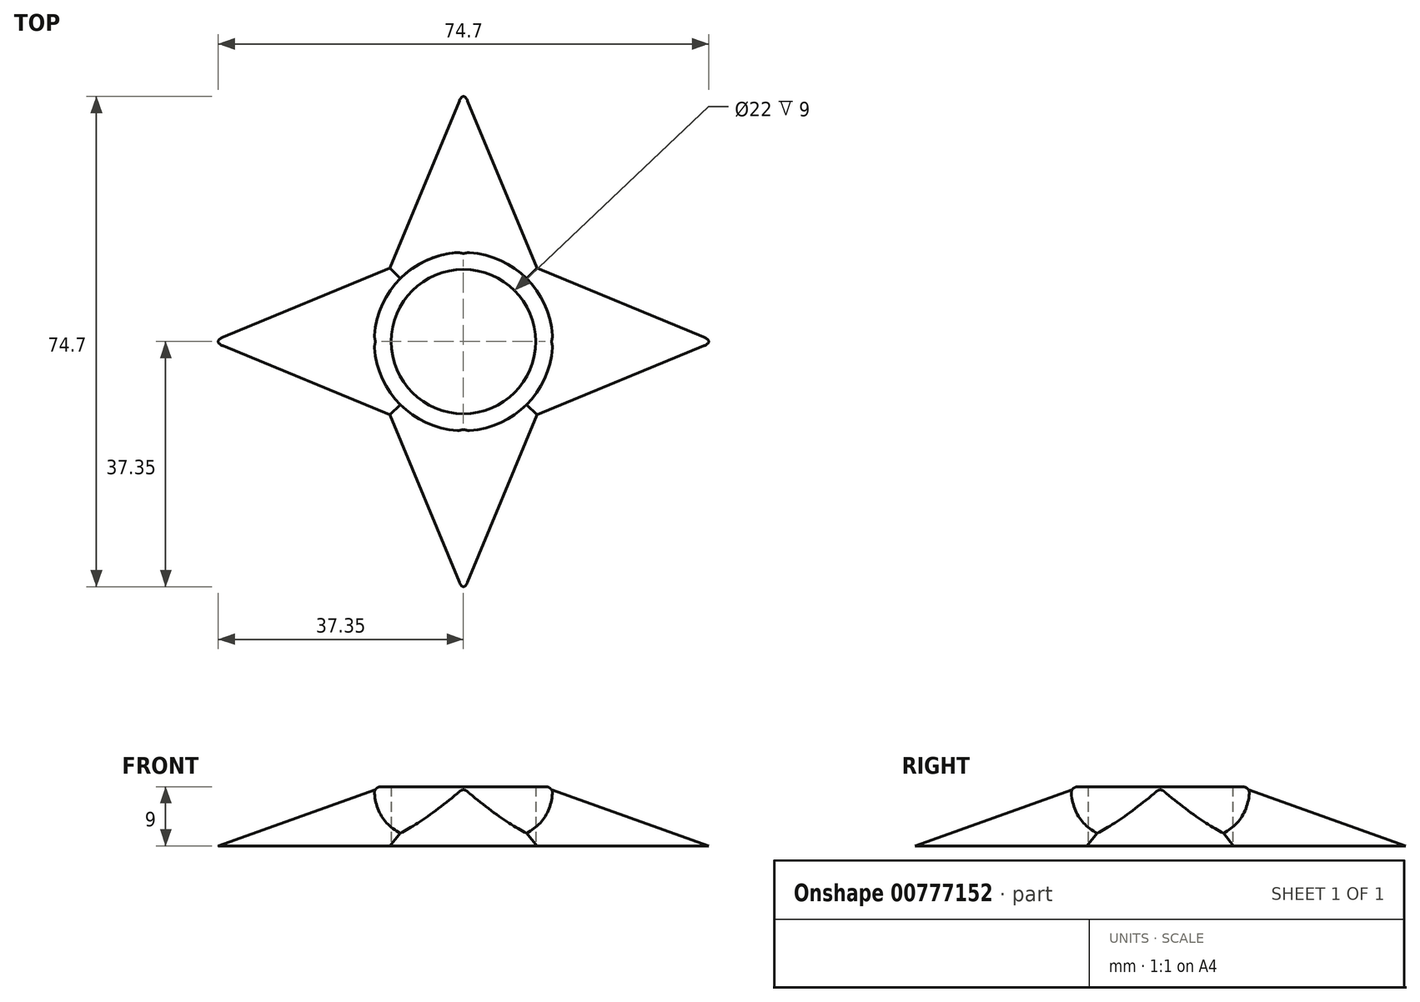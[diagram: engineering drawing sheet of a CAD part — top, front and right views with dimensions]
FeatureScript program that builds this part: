
annotation { "Feature Type Name" : "Feature", "Feature Type Description" : "" }
export const myFeature = defineFeature(function(context is Context, id is Id, definition is map)
    precondition{}
    {
        {
            var Q0;
            Q0=qCreatedBy(makeId("Top.planeOp"),FACE);
            var sketch = newSketch(context, id + "F0", { "sketchPlane" : qUnion([Q0])});
            skCircle(sketch, "E0", {"center": v(0, 0) * mm, "radius": 11 * mm});
            skCircle(sketch, "E1", {"center": v(0, 0) * mm, "radius": 13.6 * mm});
            skLineSegment(sketch, "E2", {"start": v(0, 13.6) * mm, "end": v(0, 39.05) * mm});
            skLineSegment(sketch, "E3.bottom", {"start": v(0, 0) * mm, "end": v(-11.43, 0) * mm});
            skLineSegment(sketch, "E3.top", {"start": v(0, 11.43) * mm, "end": v(-11.43, 11.43) * mm});
            skLineSegment(sketch, "E3.left", {"start": v(0, 0) * mm, "end": v(0, 11.43) * mm});
            skLineSegment(sketch, "E3.right", {"start": v(-11.43, 0) * mm, "end": v(-11.43, 11.43) * mm});
            skLineSegment(sketch, "E4", {"start": v(-11.43, 11.43) * mm, "end": v(0, 39.05) * mm});
            skLineSegment(sketch, "E5.MirrorCS", {"start": v(11.43, 11.43) * mm, "end": v(0, 39.05) * mm});
            skLineSegment(sketch, "E6.1.0", {"start": v(-11.43, 11.43) * mm, "end": v(-39.05, 0) * mm});
            skLineSegment(sketch, "E6.1.1", {"start": v(-11.43, -11.43) * mm, "end": v(-39.05, 0) * mm});
            skLineSegment(sketch, "E6.2.0", {"start": v(-11.43, -11.43) * mm, "end": v(0, -39.05) * mm});
            skLineSegment(sketch, "E6.2.1", {"start": v(11.43, -11.43) * mm, "end": v(0, -39.05) * mm});
            skLineSegment(sketch, "E6.3.0", {"start": v(11.43, -11.43) * mm, "end": v(39.05, 0) * mm});
            skLineSegment(sketch, "E6.3.1", {"start": v(11.43, 11.43) * mm, "end": v(39.05, 0) * mm});
            skSolve(sketch);
        }
        {
            var Q0;
            Q0=makeQuery(id+"F0.imprint","IMPRINT",FACE,{"disambiguationData":[TD([[makeQuery(id+"F0.imprint","IMPRINT",EDGE,{"derivedFrom":sQuery(id+"F0.wireOp",EDGE,"E2")}),1.0]])]});
            var Q1;
            {var subQ6=sQuery(id+"F0.wireOp",EDGE,"E2");Q1=makeQuery(id+"F0.imprint","IMPRINT",FACE,{"disambiguationData":[TD([[makeQuery(id+"F0.imprint","IMPRINT",EDGE,{"derivedFrom":subQ6}),-1.0]])]});}
            var Q2;
            {var subQ1=sQuery(id+"F0.wireOp",EDGE,"E3.top");Q2=makeQuery(id+"F0.imprint","IMPRINT",FACE,{"disambiguationData":[TD([[makeQuery(id+"F0.imprint","IMPRINT",EDGE,{"derivedFrom":subQ1}),1.0]])]});}
            extrude(context, id + "F1", {"entities" : qUnion([Q0, Q1, Q2]), "depth" : 8.7 * mm, "offsetDistance" : 25 * mm});
        }
        {
            var Q0;
            {var subQ0=sQuery(id+"F0.wireOp",EDGE,"E3.bottom");var subQ1=sQuery(id+"F0.wireOp",EDGE,"E0");var subQ2=makeQuery(id+"F0.imprint","INTERSECT",VERTEX,{"derivedFrom":[subQ1,subQ0]});Q0=makeQuery(id+"F0.imprint","IMPRINT",FACE,{"disambiguationData":[TD([[makeQuery(id+"F0.imprint","IMPRINT",EDGE,{"disambiguationData":[TD([[subQ2,1.0]])],"derivedFrom":subQ1}),-1.0]])]});}
            var Q1;
            {var subQ0=sQuery(id+"F0.wireOp",EDGE,"E3.bottom");var subQ1=sQuery(id+"F0.wireOp",EDGE,"E0");var subQ2=makeQuery(id+"F0.imprint","INTERSECT",VERTEX,{"derivedFrom":[subQ1,subQ0]});Q1=makeQuery(id+"F0.imprint","IMPRINT",FACE,{"disambiguationData":[TD([[makeQuery(id+"F0.imprint","IMPRINT",EDGE,{"disambiguationData":[TD([[subQ2,-1.0]])],"derivedFrom":subQ1}),-1.0]])]});}
            extrude(context, id + "F2", {"entities" : qUnion([Q0, Q1]), "operationType" : NewBodyOperationType.ADD, "depth" : 9 * mm, "offsetDistance" : 25 * mm});
        }
        {
            var Q0;
            Q0=makeQuery(id+"F1.opExtrude","CAP_EDGE",EDGE,{"disambiguationData":[OSD([sQuery(id+"F0.wireOp",EDGE,"E6.1.1")])],"isStart":false});
            var Q1;
            Q1=makeQuery(id+"F1.opExtrude","CAP_EDGE",EDGE,{"disambiguationData":[OSD([sQuery(id+"F0.wireOp",EDGE,"E6.1.0")])],"isStart":false});
            var Q2;
            Q2=makeQuery(id+"F1.opExtrude","CAP_EDGE",EDGE,{"disambiguationData":[OSD([sQuery(id+"F0.wireOp",EDGE,"E4")])],"isStart":false});
            var Q3;
            Q3=makeQuery(id+"F1.opExtrude","CAP_EDGE",EDGE,{"disambiguationData":[OSD([sQuery(id+"F0.wireOp",EDGE,"E5.MirrorCS")])],"isStart":false});
            var Q4;
            Q4=makeQuery(id+"F1.opExtrude","CAP_EDGE",EDGE,{"disambiguationData":[OSD([sQuery(id+"F0.wireOp",EDGE,"E6.3.1")])],"isStart":false});
            var Q5;
            Q5=makeQuery(id+"F1.opExtrude","CAP_EDGE",EDGE,{"disambiguationData":[OSD([sQuery(id+"F0.wireOp",EDGE,"E6.3.0")])],"isStart":false});
            var Q6;
            Q6=makeQuery(id+"F1.opExtrude","CAP_EDGE",EDGE,{"disambiguationData":[OSD([sQuery(id+"F0.wireOp",EDGE,"E6.2.1")])],"isStart":false});
            var Q7;
            Q7=makeQuery(id+"F1.opExtrude","CAP_EDGE",EDGE,{"disambiguationData":[OSD([sQuery(id+"F0.wireOp",EDGE,"E6.2.0")])],"isStart":false});
            chamfer(context, id + "F3", {"entities" : qUnion([Q0, Q1, Q2, Q3, Q4, Q5, Q6, Q7]), "chamferType" : ChamferType.OFFSET_ANGLE, "width" : 9 * mm, "oppositeDirection" : false, "angle" : 47 * degree, "tangentPropagation" : true});
        }
        {
            var Q0;
            Q0=makeQuery(id+"F2.opExtrude","CAP_EDGE",EDGE,{"disambiguationData":[OSD([sQuery(id+"F0.wireOp",EDGE,"E1")])],"isStart":false});
            fillet(context, id + "F4", {"entities" : qUnion([Q0]), "radius" : 1 * mm, "tangentPropagation" : true, "allowEdgeOverflow" : false});
        }
        {
            var Q0;
            Q0=makeQuery(id+"F3.opChamfer","BLEND_EDGE",EDGE,{"blendedFrom":[makeQuery(id+"F1.opExtrude","CAP_EDGE",EDGE,{"disambiguationData":[OSD([sQuery(id+"F0.wireOp",EDGE,"E6.2.0")])],"isStart":false}),makeQuery(id+"F1.opExtrude","CAP_EDGE",EDGE,{"disambiguationData":[OSD([sQuery(id+"F0.wireOp",EDGE,"E6.2.1")])],"isStart":false})],"blendedInto":[]});
            var Q1;
            Q1=makeQuery(id+"F3.opChamfer","BLEND_EDGE",EDGE,{"blendedFrom":[makeQuery(id+"F1.opExtrude","CAP_EDGE",EDGE,{"disambiguationData":[OSD([sQuery(id+"F0.wireOp",EDGE,"E6.3.0")])],"isStart":false}),makeQuery(id+"F1.opExtrude","CAP_EDGE",EDGE,{"disambiguationData":[OSD([sQuery(id+"F0.wireOp",EDGE,"E6.3.1")])],"isStart":false})],"blendedInto":[]});
            var Q2;
            Q2=makeQuery(id+"F3.opChamfer","BLEND_EDGE",EDGE,{"blendedFrom":[makeQuery(id+"F1.opExtrude","CAP_EDGE",EDGE,{"disambiguationData":[OSD([sQuery(id+"F0.wireOp",EDGE,"E4")])],"isStart":false}),makeQuery(id+"F1.opExtrude","CAP_EDGE",EDGE,{"disambiguationData":[OSD([sQuery(id+"F0.wireOp",EDGE,"E5.MirrorCS")])],"isStart":false})],"blendedInto":[]});
            var Q3;
            Q3=makeQuery(id+"F3.opChamfer","BLEND_EDGE",EDGE,{"blendedFrom":[makeQuery(id+"F1.opExtrude","CAP_EDGE",EDGE,{"disambiguationData":[OSD([sQuery(id+"F0.wireOp",EDGE,"E6.1.0")])],"isStart":false}),makeQuery(id+"F1.opExtrude","CAP_EDGE",EDGE,{"disambiguationData":[OSD([sQuery(id+"F0.wireOp",EDGE,"E6.1.1")])],"isStart":false})],"blendedInto":[]});
            fillet(context, id + "F5", {"entities" : qUnion([Q0, Q1, Q2, Q3]), "radius" : 1 * mm, "tangentPropagation" : true, "allowEdgeOverflow" : false});
        }
    });
